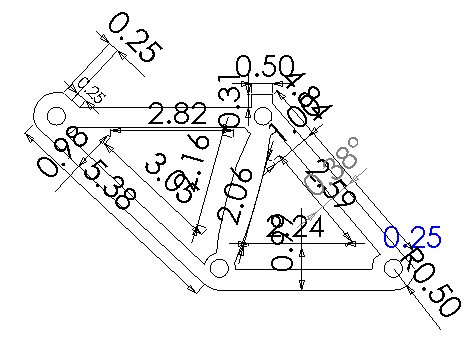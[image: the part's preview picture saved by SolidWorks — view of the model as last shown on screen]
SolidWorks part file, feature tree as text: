
SOLIDWORKS PART (.sldprt)
format: sldprt  version: not decoded by parser v0  size: 1,189,888 bytes
history: native  units: mm
features: cut_extrude x160, sketch x22, extrude x8, plane x1 (+10 scaffold rows collapsed)
feature tree (201):
  scaffold x10  (default folders/planes/origin — collapsed)
  sketch  "Sketch1"  dims[c1.D22=12.7mm c1.D1=101.6mm c1.D2=~117.207937mm c1.D3=120.65mm c1.D4=~130.41009mm c1.D5=~92.523447mm c1.D6=6.35mm c1.D7=12.7mm c1.D8=12.7mm c1.D9=~8.363444mm c2.D6=12.7mm c2.D9=12.7mm c2.D10=12.7mm c2.D11=127.0mm c2.D12=~117.207937mm c2.D13=~117.207937mm c3.D11=~126.491174mm c3.D13=~12.63756mm c3.D14=12.7mm c3.D15=12.7mm c3.D16=12.7mm c3.D17=25.4mm c3.D18=~125.494971mm c4.D17=~22.419195mm c4.D18=12.7mm c4.D19=6.35mm c4.D20=6.35mm c4.D21=~69.00021mm c4.D4=~136.76009mm c4.D6=~93.612689mm c4.D9=~114.755306mm c4.D13=~54.946304mm c4.D16=~52.298516mm c5.D17=~56.860844mm c5.D21=~65.882987mm c5.D22=101.6mm c5.D23=12.7mm c5.D9=~71.649639mm c5.D6=~7.749675mm c5.D10=~123.04911mm c5.D11=77.4458mm c5.D24=~25.172719mm c5.D25=~65.882987mm c6.D25=~0.375155deg c6.D26=~12.63756mm c6.D27=~52.298516mm c7.D27=~74.116461deg c8.D27=~65.882987mm c9.D27=~130.22614deg c10.D27=~65.882987mm c11.D27=~0.375155deg c11.D28=~65.882987mm c12.D28=~179.624845deg c13.D28=~65.882987mm c14.D28=~0.375155deg c15.D28=~62.774477mm c15.D29=~65.882987mm c16.D29=~0.375155deg c17.D29=~24.965832mm c17.D30=25.4mm]
  extrude  "Extrude1"  Depth=6.35mm
  sketch  "Sketch2"  dims[D1=120.65mm]
  cut_extrude  "Cut-Extrude1"  Depth=6.35mm cosMaterialEX=10009317
  cut_extrude  "sMaterialName"  [1 undecoded]
  cut_extrude  "cosFMVItemName"  [1 undecoded]
  cut_extrude  "cosMaterialName"  [1 undecoded]
  cut_extrude  "cosComponentName"  [1 undecoded]
  cut_extrude  "cosMaterialType"  [1 undecoded]
  cut_extrude  "cosMaterialLibFile"  [1 undecoded]
  cut_extrude  "cosMaterialRefPlaneName"  [1 undecoded]
  cut_extrude  "sMaterialSourceName"  [1 undecoded]
  cut_extrude  "sMaterialName"  [1 undecoded]
  cut_extrude  "cosFMVItemName"  [1 undecoded]
  cut_extrude  "cosMaterialName"  [1 undecoded]
  cut_extrude  "cosComponentName"  [1 undecoded]
  cut_extrude  "cosMaterialType"  [1 undecoded]
  cut_extrude  "cosMaterialLibFile"  [1 undecoded]
  cut_extrude  "cosMaterialRefPlaneName"  [1 undecoded]
  cut_extrude  "cosRestraintRefPlaneName"  [1 undecoded]
  cut_extrude  "cosFMVItemName"  [1 undecoded]
  cut_extrude  "cosLBCSymbolColor"  Depth=0 cosRestraint7=0
  cut_extrude  "cosRestraintRefPlaneName"  [1 undecoded]
  cut_extrude  "cosFMVItemName"  [1 undecoded]
  cut_extrude  "cosLBCSymbolColor"  [1 undecoded]
  cut_extrude  "cosRestraintRefPlaneName"  [1 undecoded]
  cut_extrude  "cosFMVItemName"  [1 undecoded]
  cut_extrude  "cosLBCSymbolColor"  [1 undecoded]
  cut_extrude  "cosForceRefPlaneName"  [1 undecoded]
  cut_extrude  "cosFMVItemName"  [1 undecoded]
  cut_extrude  "cosDistributionCoordSysName"  [1 undecoded]
  cut_extrude  "cosLBCSymbolColor"  Depth=0 cosForce7=0
  cut_extrude  "cosForceRefPlaneName"  [1 undecoded]
  cut_extrude  "cosFMVItemName"  [1 undecoded]
  cut_extrude  "cosDistributionCoordSysName"  [1 undecoded]
  cut_extrude  "cosLBCSymbolColor"  [1 undecoded]
  cut_extrude  "cosForceRefPlaneName"  [1 undecoded]
  cut_extrude  "cosFMVItemName"  [1 undecoded]
  cut_extrude  "cosDistributionCoordSysName"  [1 undecoded]
  cut_extrude  "cosLBCSymbolColor"  [1 undecoded]
  cut_extrude  "sMaterialSourceName"  [1 undecoded]
  cut_extrude  "sMaterialName"  [1 undecoded]
  cut_extrude  "cosFMVItemName"  [1 undecoded]
  cut_extrude  "cosMaterialName"  [1 undecoded]
  cut_extrude  "cosComponentName"  [1 undecoded]
  cut_extrude  "cosMaterialType"  [1 undecoded]
  cut_extrude  "cosMaterialLibFile"  [1 undecoded]
  cut_extrude  "cosMaterialRefPlaneName"  [1 undecoded]
  cut_extrude  "cosRestraintRefPlaneName"  [1 undecoded]
  cut_extrude  "cosFMVItemName"  [1 undecoded]
  cut_extrude  "cosLBCSymbolColor"  [1 undecoded]
  cut_extrude  "cosRestraintRefPlaneName"  [1 undecoded]
  cut_extrude  "cosFMVItemName"  [1 undecoded]
  cut_extrude  "cosLBCSymbolColor"  [1 undecoded]
  cut_extrude  "cosForceRefPlaneName"  [1 undecoded]
  cut_extrude  "cosFMVItemName"  [1 undecoded]
  cut_extrude  "cosDistributionCoordSysName"  [1 undecoded]
  cut_extrude  "cosLBCSymbolColor"  [1 undecoded]
  cut_extrude  "cosForceRefPlaneName"  [1 undecoded]
  cut_extrude  "cosFMVItemName"  [1 undecoded]
  cut_extrude  "cosDistributionCoordSysName"  [1 undecoded]
  cut_extrude  "cosLBCSymbolColor"  [1 undecoded]
  sketch  "Sketch4"
  cut_extrude  "Cut-Extrude5"  Depth=10mm
  sketch  "Sketch5"  dims[c1.D3=~7.775695mm c1.D1=12.7mm c1.D2=~82.708335mm c2.D1=12.7mm c2.D2=88.9mm]
  cut_extrude  "Cut-Extrude6"  [1 undecoded]
  sketch  "Sketch6"  dims[D1=~12.736036mm]
  cut_extrude  "Cut-Extrude7"  [1 undecoded]
  sketch  "Sketch7"  dims[c1.D2=~14.839552mm c1.D1=2.286mm c2.D2=~123.04911mm c3.D2=~179.624845deg c3.D1=~80.78799mm]
  cut_extrude  "Cut-Extrude11"  Depth=10mm
  sketch  "Sketch8"  dims[c1.D1=10.3124mm c1.D2=10.3124mm c1.D4=10.3124mm c1.D5=25.4mm c2.D1=5.08mm c2.D2=5.08mm c2.D3=~66.614782mm c3.D1=~12.472012mm c3.D2=~11.087945mm c3.D3=82.296mm c4.D2=5.08mm c4.D4=3.81mm]
  cut_extrude  "Cut-Extrude15"  Depth=10mm
  sketch  "Sketch37"  dims[c1.D1=~69.87015mm c2.D1=~179.743527deg c3.D1=~69.87015mm c4.D1=~179.743527deg c5.D1=~69.87015mm c6.D1=~0.256473deg c7.D1=~79.503313mm c8.D1=~179.743527deg c9.D1=3.81mm c9.D2=~6.457592mm]
  cut_extrude  "Cut-Extrude77"  Depth=6.35mm
  cut_extrude  "sMaterialSourceName"  [1 undecoded]
  cut_extrude  "sMaterialName"  [1 undecoded]
  cut_extrude  "cosFMVItemName"  [1 undecoded]
  cut_extrude  "cosMaterialName"  [1 undecoded]
  cut_extrude  "cosComponentName"  [1 undecoded]
  cut_extrude  "cosMaterialType"  [1 undecoded]
  cut_extrude  "cosMaterialLibFile"  [1 undecoded]
  cut_extrude  "cosMaterialRefPlaneName"  [1 undecoded]
  cut_extrude  "cosRestraintRefPlaneName"  [1 undecoded]
  cut_extrude  "cosFMVItemName"  [1 undecoded]
  cut_extrude  "cosLBCSymbolColor"  [1 undecoded]
  cut_extrude  "cosRestraintRefPlaneName"  [1 undecoded]
  cut_extrude  "cosFMVItemName"  [1 undecoded]
  cut_extrude  "cosLBCSymbolColor"  [1 undecoded]
  cut_extrude  "cosForceRefPlaneName"  [1 undecoded]
  cut_extrude  "cosFMVItemName"  [1 undecoded]
  cut_extrude  "cosDistributionCoordSysName"  [1 undecoded]
  cut_extrude  "cosLBCSymbolColor"  [1 undecoded]
  cut_extrude  "cosForceRefPlaneName"  [1 undecoded]
  cut_extrude  "cosFMVItemName"  [1 undecoded]
  cut_extrude  "cosDistributionCoordSysName"  [1 undecoded]
  cut_extrude  "cosLBCSymbolColor"  [1 undecoded]
  cut_extrude  "sMaterialSourceName"  [1 undecoded]
  cut_extrude  "sMaterialName"  [1 undecoded]
  cut_extrude  "cosFMVItemName"  [1 undecoded]
  cut_extrude  "cosMaterialName"  [1 undecoded]
  cut_extrude  "cosComponentName"  [1 undecoded]
  cut_extrude  "cosMaterialType"  [1 undecoded]
  cut_extrude  "cosMaterialLibFile"  [1 undecoded]
  cut_extrude  "cosMaterialRefPlaneName"  [1 undecoded]
  cut_extrude  "cosRestraintRefPlaneName"  [1 undecoded]
  cut_extrude  "cosFMVItemName"  [1 undecoded]
  cut_extrude  "cosLBCSymbolColor"  [1 undecoded]
  cut_extrude  "cosRestraintRefPlaneName"  [1 undecoded]
  cut_extrude  "cosFMVItemName"  [1 undecoded]
  cut_extrude  "cosLBCSymbolColor"  [1 undecoded]
  cut_extrude  "cosForceRefPlaneName"  [1 undecoded]
  cut_extrude  "cosFMVItemName"  [1 undecoded]
  cut_extrude  "cosDistributionCoordSysName"  [1 undecoded]
  cut_extrude  "cosLBCSymbolColor"  [1 undecoded]
  cut_extrude  "cosForceRefPlaneName"  [1 undecoded]
  cut_extrude  "cosFMVItemName"  [1 undecoded]
  cut_extrude  "cosDistributionCoordSysName"  [1 undecoded]
  cut_extrude  "cosLBCSymbolColor"  [1 undecoded]
  sketch  "Sketch38"
  cut_extrude  "Cut-Extrude79"  Depth=6.35mm
  sketch  "Sketch39"
  cut_extrude  "Cut-Extrude81"  Depth=6.35mm
  sketch  "Sketch40"
  extrude  "Extrude18"  Depth=6.35mm
  sketch  "Sketch41"  dims[D1=3.81mm D2=3.81mm]
  cut_extrude  "Cut-Extrude82"  Depth=7.62mm
  sketch  "Sketch43"  dims[c1.D1=~127.420455mm c2.D1=~0.501187deg]
  cut_extrude  "Cut-Extrude83"  Depth=7.62mm
  sketch  "Sketch45"
  extrude  "Extrude23"  Depth=6.35mm
  sketch  "Sketch46"
  extrude  "Extrude25"  Depth=6.35mm
  plane  "Plane9"
  sketch  "Sketch49"
  extrude  "Extrude29"  [1 undecoded]
  sketch  "Sketch50"
  cut_extrude  "Cut-Extrude84"  Depth=6.35mm
  sketch  "Sketch51"
  extrude  "Extrude30"  Depth=2.54mm
  sketch  "Sketch52"
  cut_extrude  "Cut-Extrude86"  Depth=7.62mm
  sketch  "Sketch53"
  cut_extrude  "Cut-Extrude88"  Depth=6.35mm
  sketch  "Sketch54"
  extrude  "Extrude31"  Depth=6.35mm
  sketch  "Sketch55"
  extrude  "Extrude32"  Depth=6.35mm
  cut_extrude  "sMaterialSourceName"  [1 undecoded]
  cut_extrude  "sMaterialName"  [1 undecoded]
  cut_extrude  "cosFMVItemName"  [1 undecoded]
  cut_extrude  "cosMaterialName"  [1 undecoded]
  cut_extrude  "cosComponentName"  [1 undecoded]
  cut_extrude  "cosMaterialType"  [1 undecoded]
  cut_extrude  "cosMaterialLibFile"  [1 undecoded]
  cut_extrude  "cosMaterialRefPlaneName"  [1 undecoded]
  cut_extrude  "cosRestraintRefPlaneName"  [1 undecoded]
  cut_extrude  "cosFMVItemName"  [1 undecoded]
  cut_extrude  "cosLBCSymbolColor"  [1 undecoded]
  cut_extrude  "cosRestraintRefPlaneName"  [1 undecoded]
  cut_extrude  "cosFMVItemName"  [1 undecoded]
  cut_extrude  "cosLBCSymbolColor"  [1 undecoded]
  cut_extrude  "cosForceRefPlaneName"  [1 undecoded]
  cut_extrude  "cosFMVItemName"  [1 undecoded]
  cut_extrude  "cosDistributionCoordSysName"  [1 undecoded]
  cut_extrude  "cosLBCSymbolColor"  [1 undecoded]
  cut_extrude  "cosForceRefPlaneName"  [1 undecoded]
  cut_extrude  "cosFMVItemName"  [1 undecoded]
  cut_extrude  "cosDistributionCoordSysName"  [1 undecoded]
  cut_extrude  "cosLBCSymbolColor"  [1 undecoded]
  cut_extrude  "sMaterialSourceName"  [1 undecoded]
  cut_extrude  "sMaterialName"  [1 undecoded]
  cut_extrude  "cosFMVItemName"  [1 undecoded]
  cut_extrude  "cosMaterialName"  [1 undecoded]
  cut_extrude  "cosComponentName"  [1 undecoded]
  cut_extrude  "cosMaterialType"  [1 undecoded]
  cut_extrude  "cosMaterialLibFile"  [1 undecoded]
  cut_extrude  "cosMaterialRefPlaneName"  [1 undecoded]
  cut_extrude  "cosRestraintRefPlaneName"  [1 undecoded]
  cut_extrude  "cosFMVItemName"  [1 undecoded]
  cut_extrude  "cosLBCSymbolColor"  [1 undecoded]
  cut_extrude  "cosRestraintRefPlaneName"  [1 undecoded]
  cut_extrude  "cosFMVItemName"  [1 undecoded]
  cut_extrude  "cosLBCSymbolColor"  [1 undecoded]
  cut_extrude  "cosForceRefPlaneName"  [1 undecoded]
  cut_extrude  "cosFMVItemName"  [1 undecoded]
  cut_extrude  "cosDistributionCoordSysName"  [1 undecoded]
  cut_extrude  "cosLBCSymbolColor"  [1 undecoded]
  cut_extrude  "cosForceRefPlaneName"  [1 undecoded]
  cut_extrude  "cosFMVItemName"  [1 undecoded]
  cut_extrude  "cosDistributionCoordSysName"  [1 undecoded]
  cut_extrude  "cosLBCSymbolColor"  Depth=0 cosFaceID=0
decode coverage: 31 of 190 modeling features carry decoded parameters
note: ~ marks probable driven/reference dimensions
note: 146 parameter values undecoded
summary: no parameter record found for 146 features
note: suppression state not decoded; provenance and decode notes live in map.json
